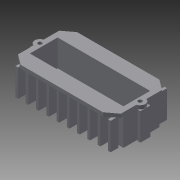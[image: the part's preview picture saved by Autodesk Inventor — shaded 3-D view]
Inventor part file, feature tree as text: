
AUTODESK INVENTOR PART (.ipt)
format: ipt  version: 2014 SP1 (Build 180222100, 222)  size: 273,408 bytes
history: native  units: in
note: dims shown in document units (in); Inventor stores cm internally (conversion verified against a paired STEP export)
features: extrude x10, sketch x9
ambient origin geometry x8: Origin, YZ Plane, XZ Plane, XY Plane, X Axis, Y Axis, Z Axis, Center Point
bodies: Solid1 (feature_tree)
feature tree (19):
  extrude  "Extrusion1"  Depth=0.875in
  extrude  "Extrusion2"  Depth=0.1in
  extrude  "Extrusion3"  Depth=0.2in TaperAngle=0.0deg
  extrude  "Extrusion15"  Depth=0.0875in TaperAngle=0.0deg
  extrude  "Extrusion16"  Depth=0.08in TaperAngle=0.0deg
  extrude  "Extrusion17"  Depth=0.01in
  extrude  "Extrusion18"  Depth=0.6625in TaperAngle=0.0deg
  extrude  "Extrusion19"  Depth=0.0875in TaperAngle=0.0deg
  extrude  "Extrusion20"  [1 undecoded]
  extrude  "Extrusion21"  [1 undecoded]
  sketch  "Sketch1"  dims[d0=2.5in d1=0.875in]
  sketch  "Sketch3"  dims[d2=0.1in d3=0.0in d4=0.1in]
  sketch  "Sketch17"  dims[d5=0.65in d6=0.0in d7=0.2in d8=0.0in]
  sketch  "Sketch18"  dims[d43=0.1in d44=0.0875in d45=0.0in]
  sketch  "Sketch19"  dims[d46=0.094in d47=0.08in d48=0.0in]
  sketch  "Sketch20"  dims[d49=0.2in d50=0.0in d51=0.01in]
  sketch  "Sketch21"  dims[d52=0.125in d53=0.0in d54=0.6625in d55=0.0in]
  sketch  "Sketch22"  dims[d56=1.375in d57=0.0875in d58=0.0in]
  sketch  "Sketch23"  dims[d59=0.6625in d60=0.0in]
note: 2 required parameter values undecoded (feature->parameter linkage not recoverable at this tier; creation-order binding heuristic only, values carry confidence <= 0.55)
